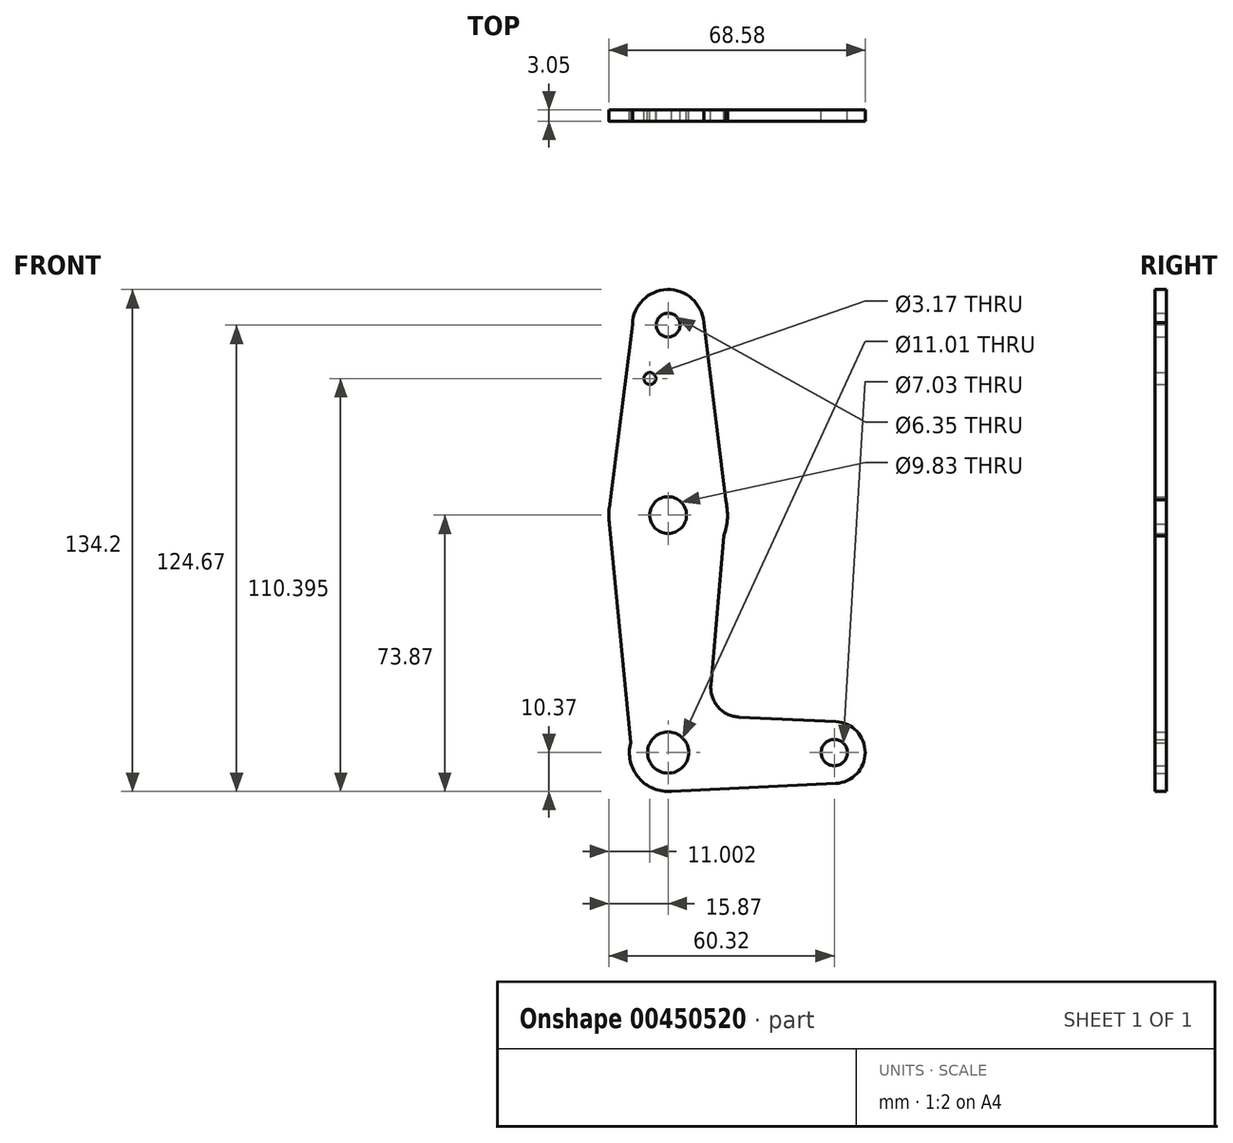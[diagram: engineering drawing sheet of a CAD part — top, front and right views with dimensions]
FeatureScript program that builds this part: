
annotation { "Feature Type Name" : "Feature", "Feature Type Description" : "" }
export const myFeature = defineFeature(function(context is Context, id is Id, definition is map)
    precondition{}
    {
        {
            var Q0;
            Q0=qCreatedBy(makeId("Front.planeOp"),FACE);
            var sketch = newSketch(context, id + "F0", { "sketchPlane" : qUnion([Q0])});
            skLineSegment(sketch, "E0", {"start": v(0, 0) * mm, "end": v(0, 63.5) * mm, "construction": true});
            skLineSegment(sketch, "E1", {"start": v(0, 63.5) * mm, "end": v(0, 114.3) * mm, "construction": true});
            skCircle(sketch, "E2", {"center": v(0, 0) * mm, "radius": 10.37 * mm});
            skCircle(sketch, "E3", {"center": v(0, 63.5) * mm, "radius": 15.88 * mm});
            skCircle(sketch, "E4", {"center": v(0, 114.3) * mm, "radius": 9.53 * mm});
            skLineSegment(sketch, "E5", {"start": v(0, 0) * mm, "end": v(44.45, 0) * mm, "construction": true});
            skCircle(sketch, "E6", {"center": v(44.45, 0) * mm, "radius": 8.26 * mm});
            skLineSegment(sketch, "E7", {"start": v(-9.52, 114.5) * mm, "end": v(-15.75, 65.5) * mm});
            skLineSegment(sketch, "E8", {"start": v(9.5, 115.03) * mm, "end": v(15.87, 63.26) * mm});
            skLineSegment(sketch, "E9", {"start": v(18.97, 9.47) * mm, "end": v(44.84, 8.25) * mm});
            skLineSegment(sketch, "E10", {"start": v(0, -10.37) * mm, "end": v(44.84, -8.25) * mm});
            skCircle(sketch, "E11", {"center": v(0, 114.3) * mm, "radius": 3.18 * mm});
            skCircle(sketch, "E12", {"center": v(0, 63.5) * mm, "radius": 4.91 * mm});
            skCircle(sketch, "E13", {"center": v(0, 0) * mm, "radius": 5.5 * mm});
            skCircle(sketch, "E14", {"center": v(44.45, 0) * mm, "radius": 3.51 * mm});
            skCircle(sketch, "E15", {"center": v(-4.87, 100.03) * mm, "radius": 1.59 * mm});
            skLineSegment(sketch, "E16", {"start": v(-15.86, 62.8) * mm, "end": v(-10.03, 2.62) * mm});
            skLineSegment(sketch, "E17", {"start": v(14.86, 57.91) * mm, "end": v(11.42, 18.1) * mm});
            skPoint(sketch, "E18.newPointA", {"position": v(0, 10.37) * mm});
            skArc(sketch, "E18.filletArc", {"start": v(11.42, 18.1) * mm, "mid": v(13.36, 12.18) * mm, "end": v(18.97, 9.47) * mm});
            skSolve(sketch);
        }
        {
            var Q0;
            Q0 = qSketchRegion(id + "F0", true);
            extrude(context, id + "F1", {"entities" : qUnion([Q0]), "depth" : 3.05 * mm});
        }
    });
